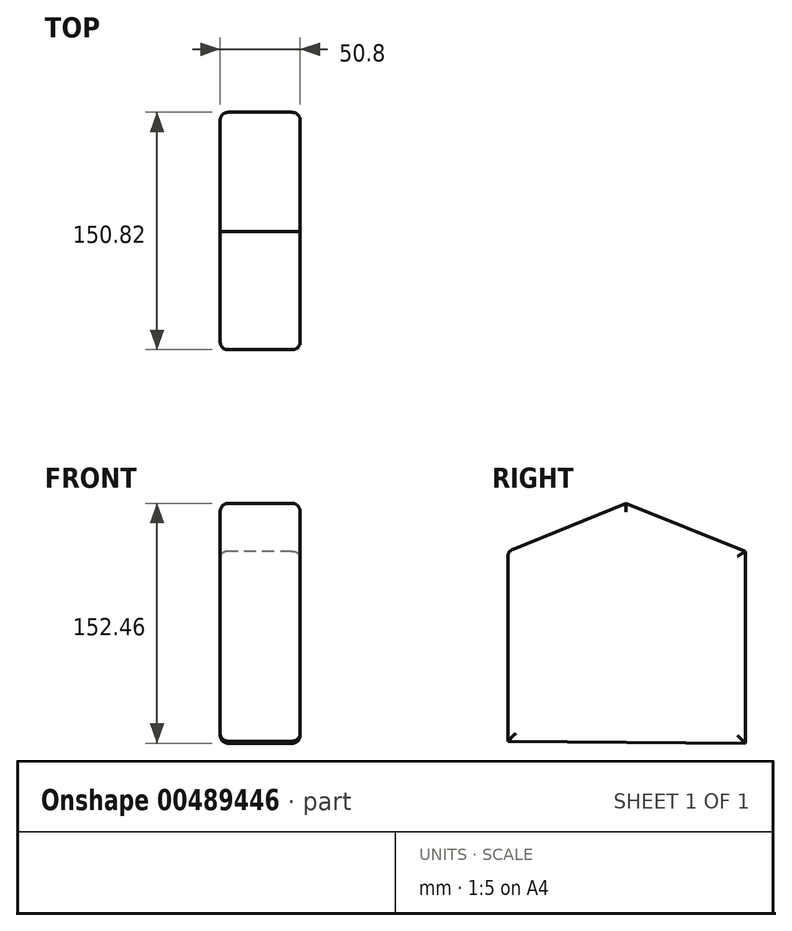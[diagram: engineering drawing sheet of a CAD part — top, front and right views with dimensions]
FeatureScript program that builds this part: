
annotation { "Feature Type Name" : "Feature", "Feature Type Description" : "" }
export const myFeature = defineFeature(function(context is Context, id is Id, definition is map)
    precondition{}
    {
        {
            var Q0;
            Q0=qCreatedBy(makeId("Right.planeOp"),FACE);
            var sketch = newSketch(context, id + "F0", { "sketchPlane" : qUnion([Q0])});
            skLineSegment(sketch, "E0", {"start": v(-75.08, -75.74) * mm, "end": v(-75.08, 44.92) * mm});
            skLineSegment(sketch, "E1", {"start": v(-75.08, 44.92) * mm, "end": v(75.74, 44.92) * mm});
            skLineSegment(sketch, "E2", {"start": v(75.74, 44.92) * mm, "end": v(75.74, -77.05) * mm});
            skLineSegment(sketch, "E3", {"start": v(75.74, -77.05) * mm, "end": v(-75.08, -75.74) * mm});
            skLineSegment(sketch, "E4", {"start": v(-75.08, 44.92) * mm, "end": v(0, 75.41) * mm});
            skLineSegment(sketch, "E5", {"start": v(0, 75.41) * mm, "end": v(75.74, 44.92) * mm});
            skLineSegment(sketch, "E6", {"start": v(-29.52, -76.14) * mm, "end": v(-29.52, 0) * mm});
            skLineSegment(sketch, "E7", {"start": v(-29.52, 0) * mm, "end": v(27.87, -0.5) * mm});
            skLineSegment(sketch, "E8", {"start": v(27.87, -0.5) * mm, "end": v(27.87, -75.74) * mm});
            skLineSegment(sketch, "E9", {"start": v(-29.52, -33.44) * mm, "end": v(27.87, -33.94) * mm});
            skLineSegment(sketch, "E10", {"start": v(0, -33.7) * mm, "end": v(0, 0) * mm});
            skLineSegment(sketch, "E11", {"start": v(27.87, -46.56) * mm, "end": v(14.75, -46.56) * mm});
            skLineSegment(sketch, "E12", {"start": v(14.75, -46.56) * mm, "end": v(14.75, -56.07) * mm});
            skLineSegment(sketch, "E13", {"start": v(14.75, -56.07) * mm, "end": v(27.87, -56.07) * mm});
            skLineSegment(sketch, "E14", {"start": v(27.87, -56.07) * mm, "end": v(27.87, -46.56) * mm});
            skLineSegment(sketch, "E15", {"start": v(-29.52, -16.72) * mm, "end": v(27.87, -17.22) * mm});
            skLineSegment(sketch, "E16", {"start": v(-75.08, 8.52) * mm, "end": v(-29.52, 8.52) * mm});
            skLineSegment(sketch, "E17", {"start": v(-29.52, 8.52) * mm, "end": v(-29.52, 37.7) * mm});
            skLineSegment(sketch, "E18", {"start": v(-29.52, 37.7) * mm, "end": v(-29.52, 44.92) * mm});
            skLineSegment(sketch, "E19", {"start": v(27.87, 44.92) * mm, "end": v(27.87, 8.52) * mm});
            skLineSegment(sketch, "E20", {"start": v(27.87, 8.52) * mm, "end": v(75.74, 8.52) * mm});
            skLineSegment(sketch, "E21", {"start": v(51.15, 44.92) * mm, "end": v(51.8, 8.52) * mm});
            skLineSegment(sketch, "E22", {"start": v(27.87, 26.72) * mm, "end": v(75.74, 26.72) * mm});
            skLineSegment(sketch, "E23", {"start": v(-54.76, 44.92) * mm, "end": v(-52.3, 8.52) * mm});
            skLineSegment(sketch, "E24", {"start": v(-75.08, 27.21) * mm, "end": v(-29.52, 27.21) * mm});
            skSolve(sketch);
        }
        {
            var Q0;
            Q0=makeQuery(id+"F0.imprint","IMPRINT",FACE,{"disambiguationData":[TD([[makeQuery(id+"F0.imprint","IMPRINT",EDGE,{"derivedFrom":sQuery(id+"F0.wireOp",EDGE,"E11")}),-1.0]])]});
            var Q1;
            {var subQ5=sQuery(id+"F0.wireOp",EDGE,"E4");Q1=makeQuery(id+"F0.imprint","IMPRINT",FACE,{"disambiguationData":[TD([[makeQuery(id+"F0.imprint","IMPRINT",EDGE,{"derivedFrom":subQ5}),-1.0]])]});}
            var Q2;
            {var subQ0=sQuery(id+"F0.wireOp",EDGE,"E9");var subQ1=sQuery(id+"F0.wireOp",EDGE,"E6");var subQ2=makeQuery(id+"F0.imprint","INTERSECT",VERTEX,{"derivedFrom":[subQ1,subQ0]});Q2=makeQuery(id+"F0.imprint","IMPRINT",FACE,{"disambiguationData":[TD([[makeQuery(id+"F0.imprint","IMPRINT",EDGE,{"disambiguationData":[TD([[subQ2,-1.0]])],"derivedFrom":subQ1}),-1.0]])]});}
            var Q3;
            {var subQ0=sQuery(id+"F0.wireOp",EDGE,"E7");var subQ1=sQuery(id+"F0.wireOp",EDGE,"E6");var subQ2=makeQuery(id+"F0.imprint","INTERSECT",VERTEX,{"derivedFrom":[subQ1,subQ0]});Q3=makeQuery(id+"F0.imprint","IMPRINT",FACE,{"disambiguationData":[TD([[makeQuery(id+"F0.imprint","IMPRINT",EDGE,{"disambiguationData":[TD([[subQ2,1.0]])],"derivedFrom":subQ1}),-1.0]])]});}
            var Q4;
            {var subQ0=sQuery(id+"F0.wireOp",EDGE,"E17");var subQ1=sQuery(id+"F0.wireOp",EDGE,"E16");var subQ2=makeQuery(id+"F0.imprint","INTERSECT",VERTEX,{"derivedFrom":[subQ1,subQ0]});Q4=makeQuery(id+"F0.imprint","IMPRINT",FACE,{"disambiguationData":[TD([[makeQuery(id+"F0.imprint","IMPRINT",EDGE,{"disambiguationData":[TD([[subQ2,1.0]])],"derivedFrom":subQ1}),1.0]])]});}
            var Q5;
            {var subQ0=sQuery(id+"F0.wireOp",EDGE,"E18");Q5=makeQuery(id+"F0.imprint","IMPRINT",FACE,{"disambiguationData":[TD([[makeQuery(id+"F0.imprint","IMPRINT",EDGE,{"derivedFrom":subQ0}),1.0]])]});}
            var Q6;
            {var subQ0=sQuery(id+"F0.wireOp",EDGE,"E1");var subQ5=sQuery(id+"F0.wireOp",EDGE,"E23");var subQ6=makeQuery(id+"F0.imprint","INTERSECT",VERTEX,{"derivedFrom":[subQ0,subQ5]});Q6=makeQuery(id+"F0.imprint","IMPRINT",FACE,{"disambiguationData":[TD([[makeQuery(id+"F0.imprint","IMPRINT",EDGE,{"disambiguationData":[TD([[subQ6,-1.0]])],"derivedFrom":subQ5}),-1.0]])]});}
            var Q7;
            {var subQ0=sQuery(id+"F0.wireOp",EDGE,"E16");var subQ1=sQuery(id+"F0.wireOp",EDGE,"E0");var subQ2=makeQuery(id+"F0.imprint","INTERSECT",VERTEX,{"derivedFrom":[subQ1,subQ0]});Q7=makeQuery(id+"F0.imprint","IMPRINT",FACE,{"disambiguationData":[TD([[makeQuery(id+"F0.imprint","IMPRINT",EDGE,{"disambiguationData":[TD([[subQ2,-1.0]])],"derivedFrom":subQ1}),-1.0]])]});}
            var Q8;
            {var subQ0=sQuery(id+"F0.wireOp",EDGE,"E20");var subQ1=sQuery(id+"F0.wireOp",EDGE,"E19");var subQ2=makeQuery(id+"F0.imprint","INTERSECT",VERTEX,{"derivedFrom":[subQ1,subQ0]});Q8=makeQuery(id+"F0.imprint","IMPRINT",FACE,{"disambiguationData":[TD([[makeQuery(id+"F0.imprint","IMPRINT",EDGE,{"disambiguationData":[TD([[subQ2,1.0]])],"derivedFrom":subQ1}),1.0]])]});}
            var Q9;
            {var subQ0=sQuery(id+"F0.wireOp",EDGE,"E19");var subQ1=sQuery(id+"F0.wireOp",EDGE,"E1");var subQ2=makeQuery(id+"F0.imprint","INTERSECT",VERTEX,{"derivedFrom":[subQ1,subQ0]});Q9=makeQuery(id+"F0.imprint","IMPRINT",FACE,{"disambiguationData":[TD([[makeQuery(id+"F0.imprint","IMPRINT",EDGE,{"disambiguationData":[TD([[subQ2,-1.0]])],"derivedFrom":subQ1}),-1.0]])]});}
            var Q10;
            {var subQ1=sQuery(id+"F0.wireOp",EDGE,"E1");var subQ3=sQuery(id+"F0.wireOp",EDGE,"E21");var subQ4=makeQuery(id+"F0.imprint","INTERSECT",VERTEX,{"derivedFrom":[subQ1,subQ3]});Q10=makeQuery(id+"F0.imprint","IMPRINT",FACE,{"disambiguationData":[TD([[makeQuery(id+"F0.imprint","IMPRINT",EDGE,{"disambiguationData":[TD([[subQ4,-1.0]])],"derivedFrom":subQ3}),1.0]])]});}
            var Q11;
            {var subQ0=sQuery(id+"F0.wireOp",EDGE,"E20");var subQ1=sQuery(id+"F0.wireOp",EDGE,"E2");var subQ2=makeQuery(id+"F0.imprint","INTERSECT",VERTEX,{"derivedFrom":[subQ1,subQ0]});Q11=makeQuery(id+"F0.imprint","IMPRINT",FACE,{"disambiguationData":[TD([[makeQuery(id+"F0.imprint","IMPRINT",EDGE,{"disambiguationData":[TD([[subQ2,1.0]])],"derivedFrom":subQ1}),-1.0]])]});}
            var Q12;
            {var subQ0=sQuery(id+"F0.wireOp",EDGE,"E8");var subQ1=sQuery(id+"F0.wireOp",EDGE,"E7");var subQ2=makeQuery(id+"F0.imprint","INTERSECT",VERTEX,{"derivedFrom":[subQ1,subQ0]});Q12=makeQuery(id+"F0.imprint","IMPRINT",FACE,{"disambiguationData":[TD([[makeQuery(id+"F0.imprint","IMPRINT",EDGE,{"disambiguationData":[TD([[subQ2,1.0]])],"derivedFrom":subQ1}),-1.0]])]});}
            var Q13;
            {var subQ0=sQuery(id+"F0.wireOp",EDGE,"E9");var subQ1=sQuery(id+"F0.wireOp",EDGE,"E8");var subQ2=makeQuery(id+"F0.imprint","INTERSECT",VERTEX,{"derivedFrom":[subQ1,subQ0]});Q13=makeQuery(id+"F0.imprint","IMPRINT",FACE,{"disambiguationData":[TD([[makeQuery(id+"F0.imprint","IMPRINT",EDGE,{"disambiguationData":[TD([[subQ2,1.0]])],"derivedFrom":subQ1}),-1.0]])]});}
            var Q14;
            Q14=makeQuery(id+"F0.imprint","IMPRINT",FACE,{"disambiguationData":[TD([[makeQuery(id+"F0.imprint","IMPRINT",EDGE,{"derivedFrom":sQuery(id+"F0.wireOp",EDGE,"E11")}),1.0]])]});
            extrude(context, id + "F1", {"entities" : qUnion([Q0, Q1, Q2, Q3, Q4, Q5, Q6, Q7, Q8, Q9, Q10, Q11, Q12, Q13, Q14]), "depth" : 50.8 * mm});
        }
        {
            var Q0;
            Q0=makeQuery(id+"F1.opExtrude","CAP_EDGE",EDGE,{"disambiguationData":[OSD([sQuery(id+"F0.wireOp",EDGE,"E5")])],"isStart":true});
            var Q1;
            Q1=makeQuery(id+"F1.opExtrude","CAP_EDGE",EDGE,{"disambiguationData":[OSD([sQuery(id+"F0.wireOp",EDGE,"E2")])],"isStart":true});
            var Q2;
            Q2=makeQuery(id+"F1.opExtrude","CAP_EDGE",EDGE,{"disambiguationData":[OSD([sQuery(id+"F0.wireOp",EDGE,"E0")])],"isStart":true});
            var Q3;
            Q3=makeQuery(id+"F1.opExtrude","CAP_EDGE",EDGE,{"disambiguationData":[OSD([sQuery(id+"F0.wireOp",EDGE,"E4")])],"isStart":true});
            var Q4;
            Q4=makeQuery(id+"F1.opExtrude","SWEPT_EDGE",EDGE,{"disambiguationData":[OSD([sQuery(id+"F0.wireOp",EDGE,"E0"),sQuery(id+"F0.wireOp",EDGE,"E1"),sQuery(id+"F0.wireOp",EDGE,"E4")])]});
            var Q5;
            Q5=makeQuery(id+"F1.opExtrude","CAP_EDGE",EDGE,{"disambiguationData":[OSD([sQuery(id+"F0.wireOp",EDGE,"E0")])],"isStart":false});
            var Q6;
            Q6=makeQuery(id+"F1.opExtrude","CAP_EDGE",EDGE,{"disambiguationData":[OSD([sQuery(id+"F0.wireOp",EDGE,"E3")])],"isStart":true});
            var Q7;
            Q7=makeQuery(id+"F1.opExtrude","CAP_FACE",FACE,{"disambiguationData":[OSD([sQuery(id+"F0.wireOp",EDGE,"E0"),sQuery(id+"F0.wireOp",EDGE,"E2"),sQuery(id+"F0.wireOp",EDGE,"E3"),sQuery(id+"F0.wireOp",EDGE,"E4"),sQuery(id+"F0.wireOp",EDGE,"E5")])],"isStart":false});
            fillet(context, id + "F2", {"entities" : qUnion([Q0, Q1, Q2, Q3, Q4, Q5, Q6, Q7]), "radius" : 5.08 * mm, "tangentPropagation" : true, "allowEdgeOverflow" : false});
        }
    });
